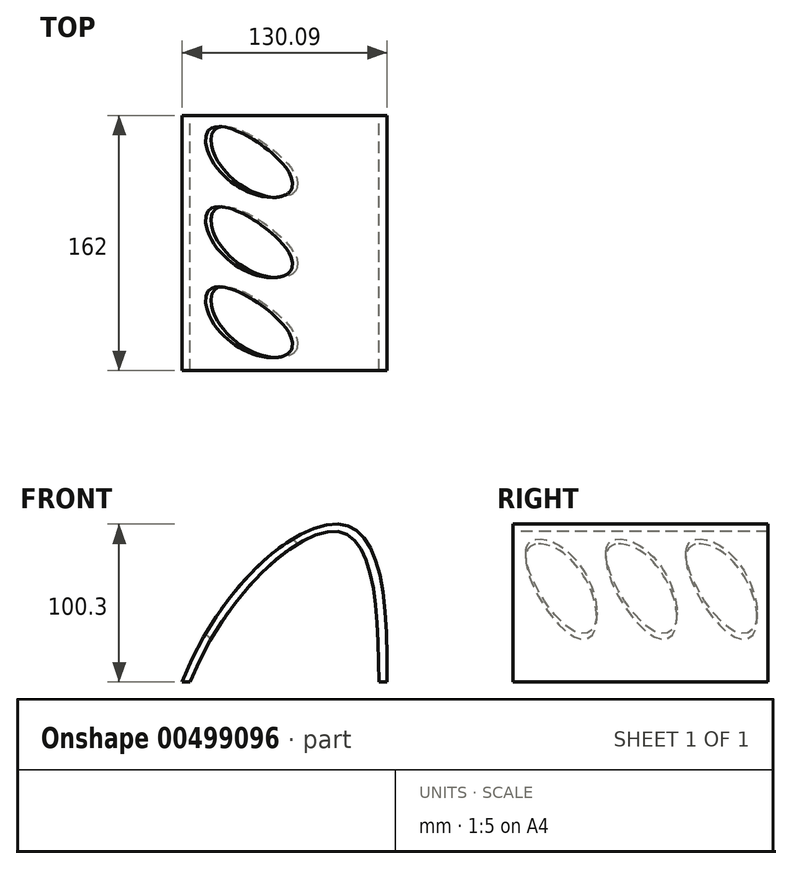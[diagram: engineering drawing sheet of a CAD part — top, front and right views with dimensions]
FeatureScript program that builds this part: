
annotation { "Feature Type Name" : "Feature", "Feature Type Description" : "" }
export const myFeature = defineFeature(function(context is Context, id is Id, definition is map)
    precondition{}
    {
        {
            var Q0;
            Q0=qCreatedBy(makeId("Front.planeOp"),FACE);
            var sketch = newSketch(context, id + "F0", { "sketchPlane" : qUnion([Q0])});
            skLineSegment(sketch, "E0", {"start": v(0, 0) * mm, "end": v(130, 0) * mm});
            skFitSpline(sketch, "E1", {"points": [v(0, 0) * mm, v(101.56, 100) * mm, v(130, 0) * mm], "startDerivative": vector(136.68, 349.14) * mm, "endDerivative": vector(-6.23, -386.27) * mm});
            skLineSegment(sketch, "E2", {"start": v(125, 0) * mm, "end": v(5, 0) * mm});
            skFitSpline(sketch, "E3", {"points": [v(125, 0) * mm, v(101.56, 95) * mm, v(5, 0) * mm], "startDerivative": vector(-2.68, 296.24) * mm, "endDerivative": vector(-125.49, -313.88) * mm});
            skSolve(sketch);
        }
        {
            var Q0;
            {var subQ0=sQuery(id+"F0.wireOp",EDGE,"E1");Q0=makeQuery(id+"F0.imprint","IMPRINT",FACE,{"disambiguationData":[TD([[makeQuery(id+"F0.imprint","IMPRINT",EDGE,{"derivedFrom":subQ0}),-1.0]])]});}
            extrude(context, id + "F1", {"entities" : qUnion([Q0]), "depth" : 162 * mm});
        }
        {
            var Q0;
            Q0=qCreatedBy(makeId("Front.planeOp"),FACE);
            var sketch = newSketch(context, id + "F2", { "sketchPlane" : qUnion([Q0])});
            skLineSegment(sketch, "E4", {"start": v(99.19, 100.47) * mm, "end": v(0, 100.47) * mm, "construction": true});
            skLineSegment(sketch, "E5", {"start": v(0, 100.47) * mm, "end": v(0, 0) * mm, "construction": true});
            skLineSegment(sketch, "E6", {"start": v(0, 0) * mm, "end": v(99.19, 100.47) * mm, "construction": true});
            skSolve(sketch);
        }
        {
            var Q0;
            Q0=sQuery(id+"F2.wireOp",EDGE,"E6");
            cPlane(context, id + "F3", {"entities" : qUnion([Q0]), "cplaneType" : CPlaneType.LINE_ANGLE, "offset" : 25 * mm, "angle" : 270 * degree, "width" : 150 * mm, "height" : 150 * mm});
        }
        {
            var Q0;
            Q0=qCreatedBy(id+"F3.planeOp",FACE);
            var sketch = newSketch(context, id + "F4", { "sketchPlane" : qUnion([Q0])});
            skEllipse(sketch, "E7", {"center": v(-29.5, 73.08) * mm, "majorRadius": 43.69 * mm, "minorRadius": 16.58 * mm, "majorAxis": v(-0.38, 0.93)});
            skEllipse(sketch, "E8.1.0.0", {"center": v(-80.4, 73.08) * mm, "majorRadius": 43.69 * mm, "minorRadius": 16.58 * mm, "majorAxis": v(-0.38, 0.93)});
            skEllipse(sketch, "E8.2.0.0", {"center": v(-131.3, 73.08) * mm, "majorRadius": 43.69 * mm, "minorRadius": 16.58 * mm, "majorAxis": v(-0.38, 0.93)});
            skLineSegment(sketch, "E8.direction1", {"start": v(-29.5, 73.08) * mm, "end": v(-80.4, 73.08) * mm, "construction": true});
            skSolve(sketch);
        }
        {
            var Q0;
            Q0=makeQuery(id+"F4.imprint","IMPRINT",FACE,{"disambiguationData":[TD([[makeQuery(id+"F4.imprint","IMPRINT",EDGE,{"derivedFrom":sQuery(id+"F4.wireOp",EDGE,"E8.2.0.0")}),1.0]])]});
            var Q1;
            Q1=makeQuery(id+"F4.imprint","IMPRINT",FACE,{"disambiguationData":[TD([[makeQuery(id+"F4.imprint","IMPRINT",EDGE,{"derivedFrom":sQuery(id+"F4.wireOp",EDGE,"E8.1.0.0")}),1.0]])]});
            var Q2;
            Q2=makeQuery(id+"F4.imprint","IMPRINT",FACE,{"disambiguationData":[TD([[makeQuery(id+"F4.imprint","IMPRINT",EDGE,{"derivedFrom":sQuery(id+"F4.wireOp",EDGE,"E7")}),1.0]])]});
            var Q3;
            Q3=sQuery(id+"F4.wireOp",EDGE,"E8.2.0.0");
            var Q4;
            Q4=sQuery(id+"F4.wireOp",EDGE,"E8.1.0.0");
            var Q5;
            Q5=sQuery(id+"F4.wireOp",EDGE,"E7");
            extrude(context, id + "F5", {"entities" : qUnion([Q0, Q1, Q2]), "operationType" : NewBodyOperationType.REMOVE, "surfaceEntities" : qUnion([Q3, Q4, Q5]), "endBound" : BoundingType.THROUGH_ALL, "oppositeDirection" : true, "depth" : 25 * mm});
        }
    });
